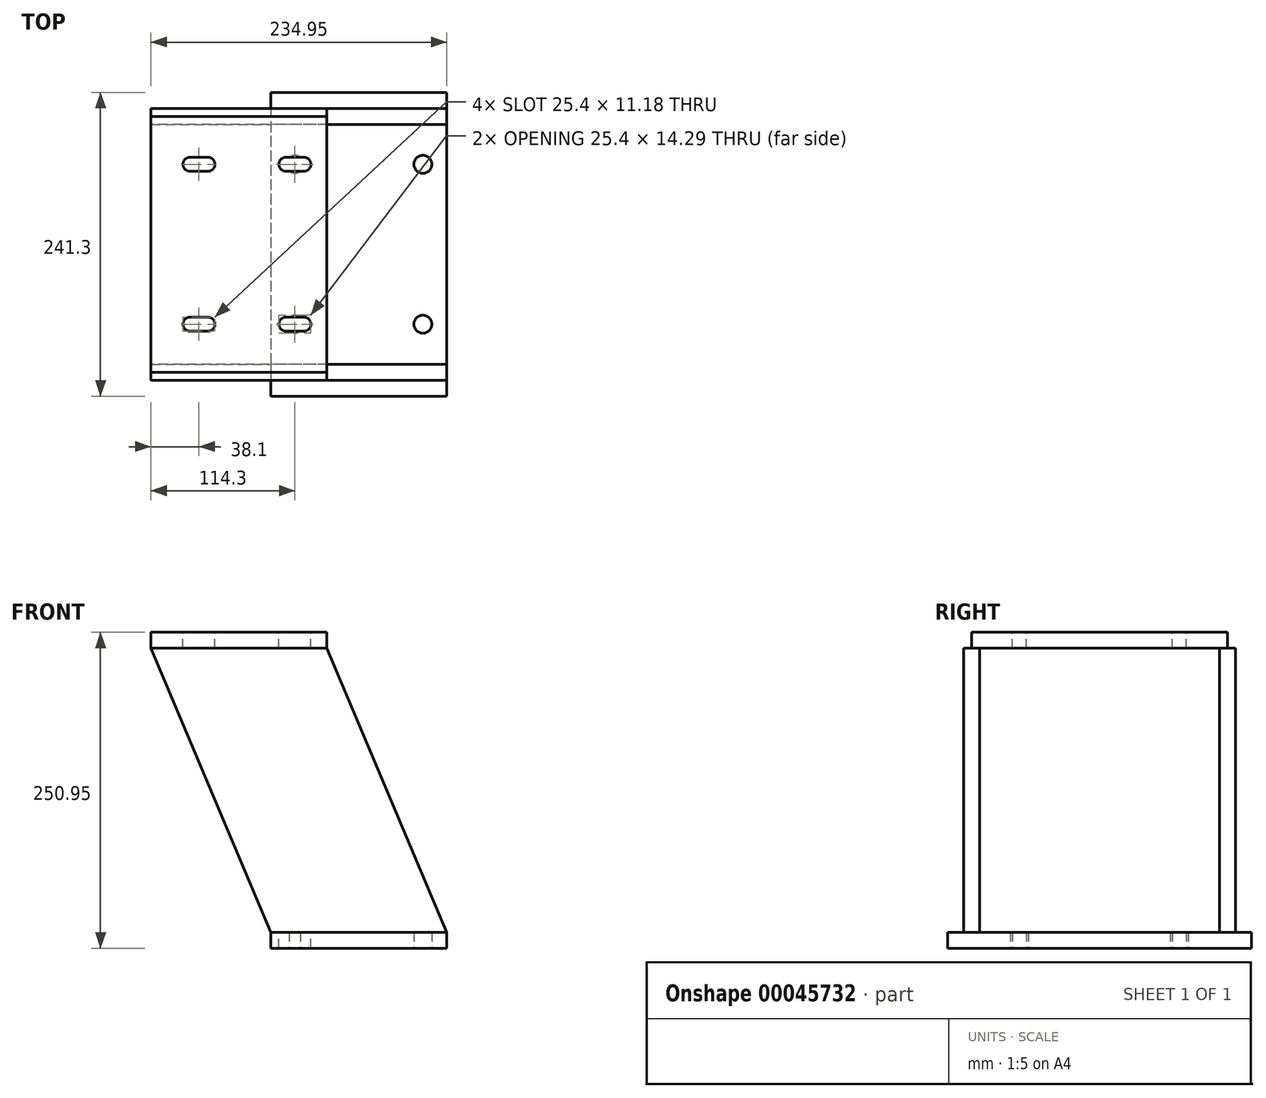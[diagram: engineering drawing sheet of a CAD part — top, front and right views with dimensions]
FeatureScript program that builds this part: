
annotation { "Feature Type Name" : "Feature", "Feature Type Description" : "" }
export const myFeature = defineFeature(function(context is Context, id is Id, definition is map)
    precondition{}
    {
        {
            var Q0;
            Q0=qCreatedBy(makeId("Top.planeOp"),FACE);
            var sketch = newSketch(context, id + "F0", { "sketchPlane" : qUnion([Q0])});
            skLineSegment(sketch, "E0.rect.bottom", {"start": v(-69.85, 120.65) * mm, "end": v(69.85, 120.65) * mm});
            skLineSegment(sketch, "E0.rect.top", {"start": v(-69.85, -120.65) * mm, "end": v(69.85, -120.65) * mm});
            skLineSegment(sketch, "E0.rect.left", {"start": v(-69.85, 120.65) * mm, "end": v(-69.85, -120.65) * mm});
            skLineSegment(sketch, "E0.rect.right", {"start": v(69.85, 120.65) * mm, "end": v(69.85, -120.65) * mm});
            skPoint(sketch, "E0.rect.middle", {"position": v(0, 0) * mm});
            skLineSegment(sketch, "E1.0", {"start": v(50.8, 120.65) * mm, "end": v(50.8, -120.65) * mm, "construction": true});
            skLineSegment(sketch, "E2.0", {"start": v(-50.8, 120.65) * mm, "end": v(-50.8, -120.65) * mm, "construction": true});
            skLineSegment(sketch, "E3", {"start": v(-106.44, 0) * mm, "end": v(168.4, 0) * mm, "construction": true});
            skLineSegment(sketch, "E4.0", {"start": v(-106.44, 63.5) * mm, "end": v(168.4, 63.5) * mm, "construction": true});
            skCircle(sketch, "E5", {"center": v(-50.8, 63.5) * mm, "radius": 7.14 * mm});
            skCircle(sketch, "E6", {"center": v(50.8, 63.5) * mm, "radius": 7.14 * mm});
            skCircle(sketch, "E7.MirrorC", {"center": v(-50.8, -63.5) * mm, "radius": 7.14 * mm});
            skCircle(sketch, "E8.MirrorC", {"center": v(50.8, -63.5) * mm, "radius": 7.14 * mm});
            skSolve(sketch);
        }
        {
            var Q0;
            Q0=qSketchRegion(id+"F0",true);
            extrude(context, id + "F1", {"entities" : qUnion([Q0]), "depth" : 12.7 * mm});
        }
        {
            var Q0;
            Q0=makeQuery(id+"F1.opExtrude","CAP_FACE",FACE,{"disambiguationData":[OSD([sQuery(id+"F0.wireOp",EDGE,"E0.rect.bottom"),sQuery(id+"F0.wireOp",EDGE,"E0.rect.top"),sQuery(id+"F0.wireOp",EDGE,"E0.rect.left"),sQuery(id+"F0.wireOp",EDGE,"E0.rect.right"),sQuery(id+"F0.wireOp",EDGE,"E5"),sQuery(id+"F0.wireOp",EDGE,"E6"),sQuery(id+"F0.wireOp",EDGE,"E7.MirrorC"),sQuery(id+"F0.wireOp",EDGE,"E8.MirrorC")])],"isStart":false});
            var sketch = newSketch(context, id + "F2", { "sketchPlane" : qUnion([Q0])});
            skLineSegment(sketch, "E9.bottom", {"start": v(69.85, -95.25) * mm, "end": v(-165.1, -95.25) * mm});
            skLineSegment(sketch, "E9.top", {"start": v(69.85, -107.95) * mm, "end": v(-165.1, -107.95) * mm});
            skLineSegment(sketch, "E9.left", {"start": v(69.85, -95.25) * mm, "end": v(69.85, -107.95) * mm});
            skLineSegment(sketch, "E9.right", {"start": v(-165.1, -95.25) * mm, "end": v(-165.1, -107.95) * mm});
            skLineSegment(sketch, "E10", {"start": v(-155.1, 0) * mm, "end": v(166.42, 0) * mm, "construction": true});
            skLineSegment(sketch, "E11.MirrorCS", {"start": v(69.85, 95.25) * mm, "end": v(-165.1, 95.25) * mm});
            skLineSegment(sketch, "E12.MirrorCS", {"start": v(69.85, 107.95) * mm, "end": v(-165.1, 107.95) * mm});
            skLineSegment(sketch, "E13.MirrorCS", {"start": v(-165.1, 95.25) * mm, "end": v(-165.1, 107.95) * mm});
            skLineSegment(sketch, "E14.MirrorCS", {"start": v(69.85, 95.25) * mm, "end": v(69.85, 107.95) * mm});
            skLineSegment(sketch, "E15.MirrorCS", {"start": v(69.85, -107.95) * mm, "end": v(-165.1, -107.95) * mm, "construction": true});
            skLineSegment(sketch, "E16.MirrorCS", {"start": v(69.85, -95.25) * mm, "end": v(-165.1, -95.25) * mm, "construction": true});
            skLineSegment(sketch, "E17.MirrorCS", {"start": v(-165.1, -95.25) * mm, "end": v(-165.1, -107.95) * mm, "construction": true});
            skLineSegment(sketch, "E18.MirrorCS", {"start": v(69.85, -95.25) * mm, "end": v(69.85, -107.95) * mm, "construction": true});
            skSolve(sketch);
        }
        {
            var Q0;
            Q0=qSketchRegion(id+"F2",true);
            extrude(context, id + "F3", {"entities" : qUnion([Q0]), "depth" : 225.55 * mm});
        }
        {
            var Q0;
            Q0=qCreatedBy(makeId("Front.planeOp"),FACE);
            var sketch = newSketch(context, id + "F4", { "sketchPlane" : qUnion([Q0])});
            skLineSegment(sketch, "E19.0", {"start": v(69.85, 238.25) * mm, "end": v(-165.1, 238.25) * mm, "construction": true});
            skLineSegment(sketch, "E20.bottom", {"start": v(-165.1, 238.25) * mm, "end": v(-25.4, 238.25) * mm});
            skLineSegment(sketch, "E20.top", {"start": v(-165.1, 250.95) * mm, "end": v(-25.4, 250.95) * mm});
            skLineSegment(sketch, "E20.left", {"start": v(-165.1, 238.25) * mm, "end": v(-165.1, 250.95) * mm});
            skLineSegment(sketch, "E20.right", {"start": v(-25.4, 238.25) * mm, "end": v(-25.4, 250.95) * mm});
            skSolve(sketch);
        }
        {
            var Q0;
            Q0=qSketchRegion(id+"F4",true);
            extrude(context, id + "F5", {"entities" : qUnion([Q0]), "endBound" : BoundingType.SYMMETRIC, "depth" : 203.2 * mm});
        }
        {
            var Q0;
            Q0=makeQuery(id+"F3.opExtrude","SWEPT_FACE",FACE,{"disambiguationData":[OSD([sQuery(id+"F2.wireOp",EDGE,"E9.top")])]});
            var sketch = newSketch(context, id + "F6", { "sketchPlane" : qUnion([Q0])});
            skLineSegment(sketch, "E21.0", {"start": v(-69.85, 12.7) * mm, "end": v(-69.85, 0) * mm, "construction": true});
            skLineSegment(sketch, "E22.0", {"start": v(-165.1, 238.25) * mm, "end": v(-165.1, 12.7) * mm, "construction": true});
            skLineSegment(sketch, "E23.0", {"start": v(-25.4, 238.25) * mm, "end": v(-25.4, 250.95) * mm, "construction": true});
            skLineSegment(sketch, "E24.0", {"start": v(69.85, 238.25) * mm, "end": v(69.85, 12.7) * mm, "construction": true});
            skLineSegment(sketch, "E25", {"start": v(-165.1, 238.25) * mm, "end": v(-69.85, 12.7) * mm});
            skLineSegment(sketch, "E26", {"start": v(-25.4, 238.25) * mm, "end": v(69.85, 12.7) * mm});
            skLineSegment(sketch, "E27.0.0", {"start": v(-165.1, 12.7) * mm, "end": v(-69.85, 12.7) * mm});
            skLineSegment(sketch, "E27.0.1", {"start": v(69.85, 12.7) * mm, "end": v(69.85, 238.25) * mm});
            skLineSegment(sketch, "E27.0.2", {"start": v(69.85, 238.25) * mm, "end": v(-25.4, 238.25) * mm});
            skLineSegment(sketch, "E27.0.3", {"start": v(-165.1, 238.25) * mm, "end": v(-165.1, 12.7) * mm});
            skSolve(sketch);
        }
        {
            var Q0;
            Q0=qSketchRegion(id+"F6",true);
            var Q1;
            Q1=makeQuery(id+"F3.opExtrude","SWEPT_FACE",FACE,{"disambiguationData":[OSD([sQuery(id+"F2.wireOp",EDGE,"E12.MirrorCS")])]});
            extrude(context, id + "F7", {"entities" : qUnion([Q0, Q1]), "operationType" : NewBodyOperationType.REMOVE, "endBound" : BoundingType.THROUGH_ALL, "oppositeDirection" : true, "depth" : 25.4 * mm});
        }
        {
            var Q0;
            Q0=makeQuery(id+"F5.opExtrude","SWEPT_FACE",FACE,{"disambiguationData":[OSD([sQuery(id+"F4.wireOp",EDGE,"E20.top")])]});
            var sketch = newSketch(context, id + "F8", { "sketchPlane" : qUnion([Q0])});
            skLineSegment(sketch, "E28", {"start": v(-165.1, 0) * mm, "end": v(-25.4, 0) * mm, "construction": true});
            skLineSegment(sketch, "E29.0", {"start": v(-88.9, -101.6) * mm, "end": v(-88.9, 101.6) * mm, "construction": true});
            skLineSegment(sketch, "E30.0", {"start": v(-50.8, -101.6) * mm, "end": v(-50.8, 101.6) * mm, "construction": true});
            skLineSegment(sketch, "E31.0", {"start": v(-165.1, 63.5) * mm, "end": v(-25.4, 63.5) * mm, "construction": true});
            skLineSegment(sketch, "E32.0", {"start": v(-43.69, -101.6) * mm, "end": v(-43.69, 101.6) * mm, "construction": true});
            skLineSegment(sketch, "E33.0", {"start": v(-57.91, -101.6) * mm, "end": v(-57.91, 101.6) * mm, "construction": true});
            skLineSegment(sketch, "E34", {"start": v(-57.91, 63.5) * mm, "end": v(-43.69, 63.5) * mm});
            skArc(sketch, "E35.0.startCap", {"start": v(-57.91, 57.91) * mm, "mid": v(-63.5, 63.5) * mm, "end": v(-57.91, 69.09) * mm});
            skArc(sketch, "E35.0.endCap", {"start": v(-43.69, 69.09) * mm, "mid": v(-38.1, 63.5) * mm, "end": v(-43.69, 57.91) * mm});
            skLineSegment(sketch, "E35.0.left", {"start": v(-57.91, 69.09) * mm, "end": v(-43.69, 69.09) * mm});
            skLineSegment(sketch, "E35.0.right", {"start": v(-57.91, 57.91) * mm, "end": v(-43.69, 57.91) * mm});
            skLineSegment(sketch, "E36.0.1.0", {"start": v(-57.91, -63.5) * mm, "end": v(-43.69, -63.5) * mm});
            skArc(sketch, "E36.0.1.1", {"start": v(-57.91, -69.09) * mm, "mid": v(-63.5, -63.5) * mm, "end": v(-57.91, -57.91) * mm});
            skArc(sketch, "E36.0.1.2", {"start": v(-43.69, -57.91) * mm, "mid": v(-38.1, -63.5) * mm, "end": v(-43.69, -69.09) * mm});
            skLineSegment(sketch, "E36.0.1.3", {"start": v(-57.91, -57.91) * mm, "end": v(-43.69, -57.91) * mm});
            skLineSegment(sketch, "E36.0.1.4", {"start": v(-57.91, -69.09) * mm, "end": v(-43.69, -69.09) * mm});
            skLineSegment(sketch, "E36.1.0.0", {"start": v(-134.11, 63.5) * mm, "end": v(-119.89, 63.5) * mm});
            skArc(sketch, "E36.1.0.1", {"start": v(-134.11, 57.91) * mm, "mid": v(-139.7, 63.5) * mm, "end": v(-134.11, 69.09) * mm});
            skArc(sketch, "E36.1.0.2", {"start": v(-119.89, 69.09) * mm, "mid": v(-114.3, 63.5) * mm, "end": v(-119.89, 57.91) * mm});
            skLineSegment(sketch, "E36.1.0.3", {"start": v(-134.11, 69.09) * mm, "end": v(-119.89, 69.09) * mm});
            skLineSegment(sketch, "E36.1.0.4", {"start": v(-134.11, 57.91) * mm, "end": v(-119.89, 57.91) * mm});
            skLineSegment(sketch, "E36.1.1.0", {"start": v(-134.11, -63.5) * mm, "end": v(-119.89, -63.5) * mm});
            skArc(sketch, "E36.1.1.1", {"start": v(-134.11, -69.09) * mm, "mid": v(-139.7, -63.5) * mm, "end": v(-134.11, -57.91) * mm});
            skArc(sketch, "E36.1.1.2", {"start": v(-119.89, -57.91) * mm, "mid": v(-114.3, -63.5) * mm, "end": v(-119.89, -69.09) * mm});
            skLineSegment(sketch, "E36.1.1.3", {"start": v(-134.11, -57.91) * mm, "end": v(-119.89, -57.91) * mm});
            skLineSegment(sketch, "E36.1.1.4", {"start": v(-134.11, -69.09) * mm, "end": v(-119.89, -69.09) * mm});
            skLineSegment(sketch, "E36.direction1", {"start": v(-57.91, 63.5) * mm, "end": v(-134.11, 63.5) * mm, "construction": true});
            skLineSegment(sketch, "E36.direction2", {"start": v(-57.91, 63.5) * mm, "end": v(-57.91, -63.5) * mm, "construction": true});
            skSolve(sketch);
        }
        {
            var Q0;
            Q0=qSketchRegion(id+"F8",true);
            extrude(context, id + "F9", {"entities" : qUnion([Q0]), "operationType" : NewBodyOperationType.REMOVE, "endBound" : BoundingType.THROUGH_ALL, "oppositeDirection" : true, "depth" : 25.4 * mm});
        }
    });
